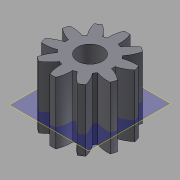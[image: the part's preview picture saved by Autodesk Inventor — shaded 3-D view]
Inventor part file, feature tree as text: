
AUTODESK INVENTOR PART (.ipt)
format: ipt  version: 2015 (Build 190159000, 159)  size: 166,400 bytes
history: native  units: in
note: dims shown in document units (in); Inventor stores cm internally (conversion verified against a paired STEP export)
features: other x13, sketch x3, plane x2
ambient origin geometry x8: Origin, YZ Plane, XZ Plane, XY Plane, X Axis, Y Axis, Z Axis, Center Point
bodies: Solid1 (feature_tree)
feature tree (18):
  other  "Spur Gear19_MIR1.ipt"
  other  "Solid1::Spur Gear19_MIR1.ipt"
  other  "TaggingFeature1"
  sketch  "Sketch1"  dims[d0=0.3937in]
  sketch  "Sketch2"  dims[d16=0.4724in d17=0.0in d41=0.0in d43=0.4724in d46=0.4724in d47=0.0in d48=0.0in]
  sketch  "Sketch3"
  plane  "XZ Plane_1"
  plane  "Work Plane2"
  other  "Z Axis_1"
  other  "Srf1"
  other  "Srf1::Derived"
  other  "Distance iMate"
  other  "Align iMate"
  other  "Mesh iMate"
  other  "Axis iMate"
  other  "Position iMate"
  other  "Mesh iMate2"
  other  "Start plane iMate"
